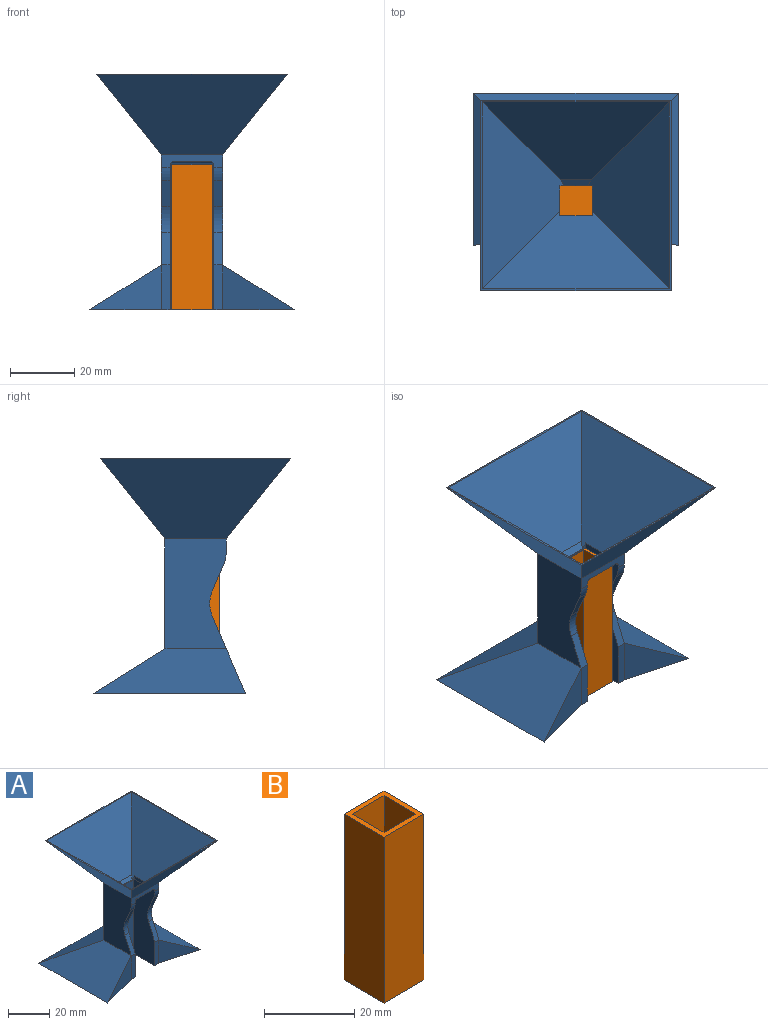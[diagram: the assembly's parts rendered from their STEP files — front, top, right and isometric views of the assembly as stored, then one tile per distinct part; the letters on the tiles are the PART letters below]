
ASSEMBLY  parts=2 mates=1
PART A: 41 faces, bbox 63.5x61.2x73 mm
  f0: plane 47.25x22.25mm, normal (-0.53,0,0.85), area 869mm2, adj f2,f13,f30,f40
  f1: plane 47.25x22.25mm, normal (0.53,0,0.85), area 869mm2, adj f3,f13,f30,f39
  f2: plane 34.1x19mm, normal (-1,0,0), area 565.6mm2, adj f0,f8,f12,f20,f33,f34,f35,f36
  f3: plane 34.1x19mm, normal (1,0,0), area 565.6mm2, adj f1,f8,f12,f14,f31,f32,f37,f38
  f4: plane 44.8x14.5mm, normal (1,0,0), area 567.4mm2, adj f7,f10,f12,f13,f28,f33,f34,f35
  f5: plane 44.8x14.5mm, normal (-1,0,0), area 567.4mm2, adj f6,f10,f12,f13,f27,f31,f32,f37
  f6: plane 13.9x2.75mm, normal (0,-1,0), area 38.2mm2, adj f5,f13,f32,f39
  f7: plane 13.9x2.75mm, normal (0,-1,0), area 38.2mm2, adj f4,f13,f33,f40
  f8: plane 34.1x19mm, normal (0,1,0), area 647.9mm2, adj f2,f3,f17,f30
  f9: plane 10x2mm, normal (0,-1,0), area 7.2mm2, adj f15,f21,f23,f24,f25,f26
  f10: plane 44.8x13.5mm, normal (0,-1,0), area 604.8mm2, adj f4,f5,f13,f29
  f11: plane 58x25mm, normal (0,0.72,0.69), area 1160.2mm2, adj f15,f19,f21,f22,f23,f24
  f12: plane 19x3.95mm, normal (0,-1,0), area 49.4mm2, adj f2,f3,f4,f5,f16,f25,f27,f28
  f13: plane 63.5x47.25mm, normal (0,0,-1), area 2556.7mm2, adj f0,f1,f4,f5,f6,f7,f10,f30
  f14: plane 59x25mm, normal (0.78,0,-0.62), area 1248.6mm2, adj f3,f16,f17,f19
  f15: plane 58x26.5mm, normal (-0.72,0,0.69), area 1180.4mm2, adj f9,f11,f18,f19,f24,f26
  f16: plane 59x25mm, normal (0,-0.78,-0.62), area 1248.6mm2, adj f12,f14,f19,f20
  f17: plane 59x25mm, normal (0,0.78,-0.62), area 1248.6mm2, adj f8,f14,f19,f20
  f18: plane 58x25.16mm, normal (0,-0.72,0.69), area 1180.4mm2, adj f15,f19,f21,f26
  f19: plane 59x59mm, normal (0,0,1), area 117mm2, adj f11,f14,f15,f16,f17,f18,f20,f21
  f20: plane 59x25mm, normal (-0.78,0,-0.62), area 1248.6mm2, adj f2,f16,f17,f19
  f21: plane 58x26.5mm, normal (0.72,0,0.69), area 1180.4mm2, adj f9,f11,f18,f19,f23,f26
  f22: plane 10x3.3mm, normal (0,1,0), area 33mm2, adj f11,f23,f24,f25
  f23: plane 9.25x3.3mm, normal (1,0,0), area 19.3mm2, adj f9,f11,f21,f22,f25
  f24: plane 9.25x3.3mm, normal (-1,0,0), area 19.3mm2, adj f9,f11,f15,f22,f25
  f25: plane 13.3x11.1mm, normal (0,0,-1), area 55.1mm2, adj f9,f12,f22,f23,f24,f27,f28,f29
  f26: plane 9.7x1.85mm, normal (0,-0.59,0.81), area 19.2mm2, adj f9,f15,f18,f21
  f27: cylinder r=1.2mm len=14.5mm, axis (0,-1,0), area 26.5mm2, adj f5,f12,f25,f29
  f28: cylinder r=1.2mm len=14.5mm, axis (0,1,0), area 26.5mm2, adj f4,f12,f25,f29
  f29: cylinder r=1.2mm len=13.5mm, axis (1,0,0), area 23.8mm2, adj f10,f25,f27,f28
  f30: plane 63.5x22.25mm, normal (0,0.53,0.85), area 1082.1mm2, adj f0,f1,f8,f13
  f31: plane 8.24x3.52mm, normal (0,-0.92,-0.39), area 24.6mm2, adj f3,f5,f37,f38
  f32: plane 10.12x4.32mm, normal (0,-0.92,0.39), area 30.3mm2, adj f3,f5,f6,f38
  f33: plane 10.12x4.32mm, normal (0,-0.92,0.39), area 30.3mm2, adj f2,f4,f7,f35
  f34: plane 8.24x3.52mm, normal (0,-0.92,-0.39), area 24.6mm2, adj f2,f4,f35,f36
  f35: cylinder r=10mm len=7.86mm, axis (1,0,0), area 22.2mm2, adj f2,f4,f33,f34
  f36: cylinder r=10mm len=3.93mm, axis (-1,0,0), area 11.1mm2, adj f2,f4,f12,f34
  f37: cylinder r=10mm len=3.93mm, axis (-1,0,0), area 11.1mm2, adj f3,f5,f12,f31
  f38: cylinder r=10mm len=7.86mm, axis (1,0,0), area 22.2mm2, adj f3,f5,f31,f32
  f39: plane 22.25x13.9mm, normal (-0.26,-0.97,0), area 160.2mm2, adj f1,f6,f13
  f40: plane 22.25x13.9mm, normal (0.26,-0.97,0), area 160.2mm2, adj f0,f7,f13
PART B: 11 faces, bbox 12.5x12.5x45 mm
  f0: plane 12.5x12.5mm, normal (0,0,1), area 56.3mm2, adj f1,f3,f4,f5,f6,f8,f9,f10
  f1: plane 45x12.5mm, normal (-1,0,0), area 562.5mm2, adj f0,f2,f4,f5
  f2: plane 12.5x12.5mm, normal (0,0,-1), area 156.3mm2, adj f1,f3,f4,f5
  f3: plane 45x12.5mm, normal (1,0,0), area 562.5mm2, adj f0,f2,f4,f5
  f4: plane 45x12.5mm, normal (0,-1,0), area 562.5mm2, adj f0,f1,f2,f3
  f5: plane 45x12.5mm, normal (0,1,0), area 562.5mm2, adj f0,f1,f2,f3
  f6: plane 43.75x10mm, normal (1,0,0), area 437.5mm2, adj f0,f7,f9,f10
  f7: plane 10x10mm, normal (0,0,1), area 100mm2, adj f6,f8,f9,f10
  f8: plane 43.75x10mm, normal (-1,0,0), area 437.5mm2, adj f0,f7,f9,f10
  f9: plane 43.75x10mm, normal (0,1,0), area 437.5mm2, adj f0,f6,f7,f8
  f10: plane 43.75x10mm, normal (0,-1,0), area 437.5mm2, adj f0,f6,f7,f8
PLACE A t=(-7.36,8.35,-4.39)mm
PLACE B t=(-4.11,22.85,-4.39)mm
MATE fastened B.f2 <-> A.f13  axis (0,0,-1) through (2.14,22.85,-4.39)mm
